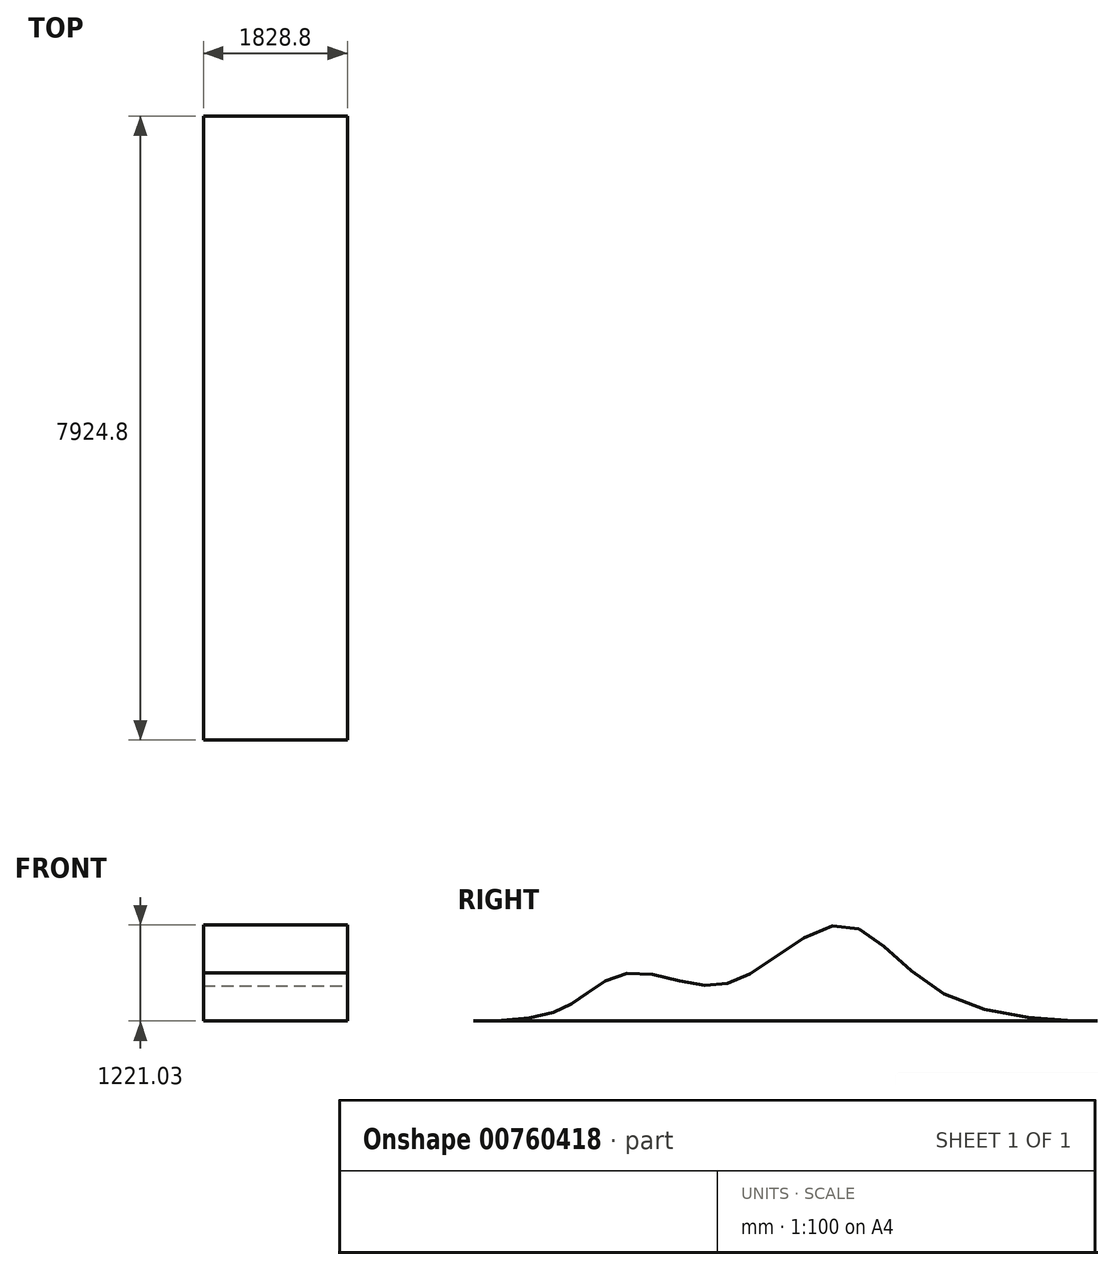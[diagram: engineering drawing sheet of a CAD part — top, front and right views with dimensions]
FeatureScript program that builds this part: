
annotation { "Feature Type Name" : "Feature", "Feature Type Description" : "" }
export const myFeature = defineFeature(function(context is Context, id is Id, definition is map)
    precondition{}
    {
        {
            var Q0;
            Q0=qCreatedBy(makeId("Right.planeOp"),FACE);
            var sketch = newSketch(context, id + "F0", { "sketchPlane" : qUnion([Q0])});
            skLineSegment(sketch, "E0", {"start": v(-964.37, -1219.2) * mm, "end": v(6960.43, -1219.2) * mm});
            skFitSpline(sketch, "E1", {"points": [v(-964.37, -1219.2) * mm, v(0, -1127.48) * mm, v(455.02, -883.22) * mm, v(1016.83, -609.6) * mm, v(1931.23, -762) * mm, v(2631.78, -571.38) * mm, v(3760.03, 0) * mm, v(5013.85, -874.98) * mm, v(6960.43, -1219.2) * mm], "startDerivative": vector(7868.48, 0) * mm, "endDerivative": vector(6676, 0) * mm});
            skSolve(sketch);
        }
        {
            var Q0;
            Q0 = qSketchRegion(id + "F0", true);
            extrude(context, id + "F1", {"entities" : qUnion([Q0]), "depth" : 1828.8 * mm, "offsetDistance" : 30.48 * mm});
        }
    });
